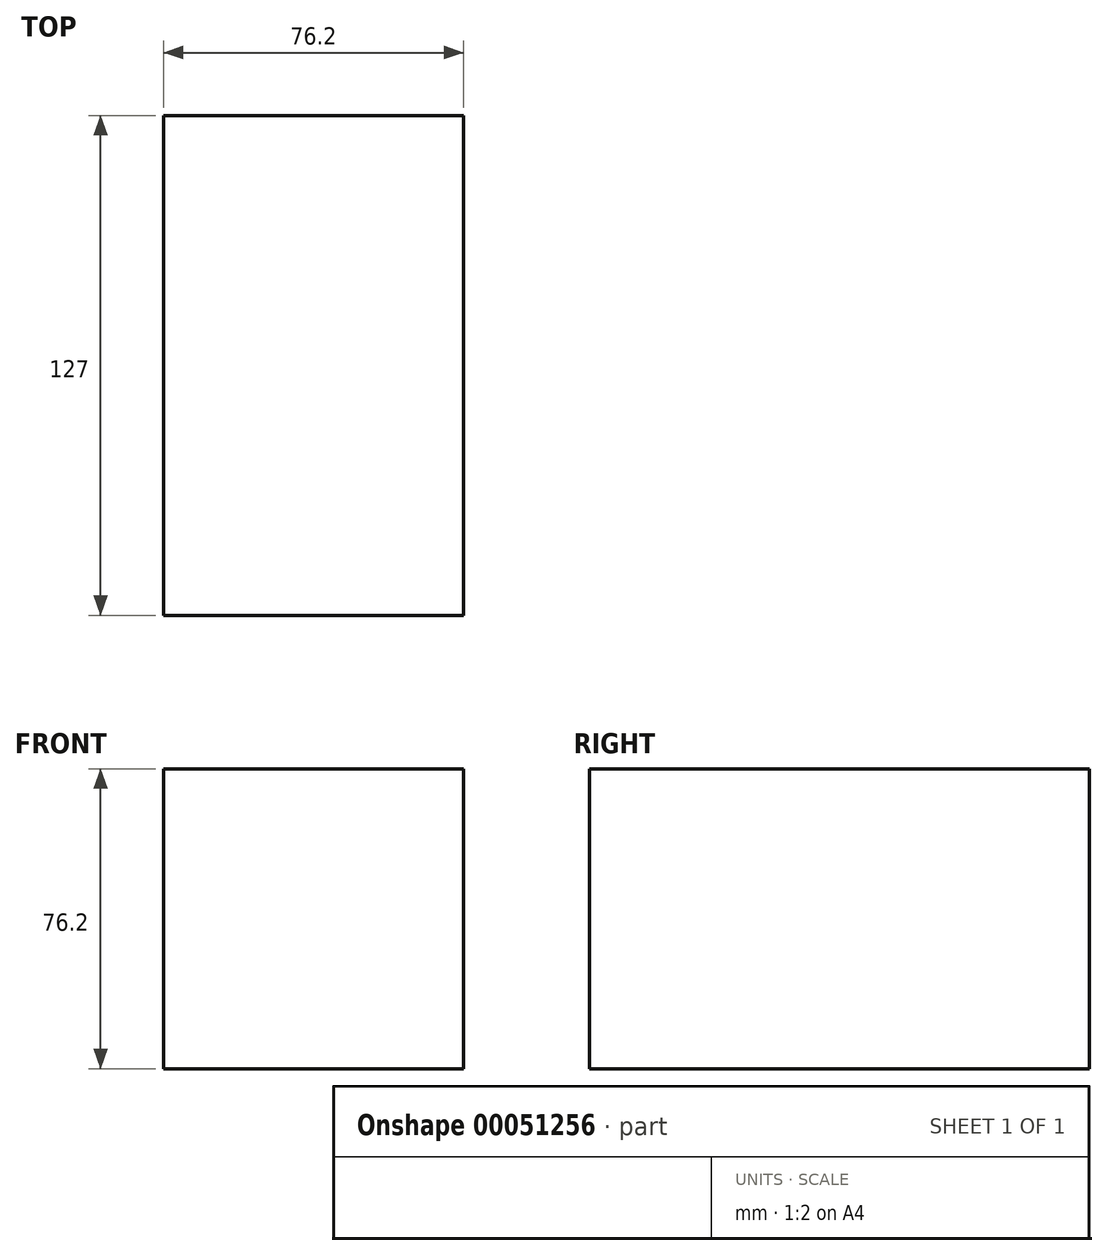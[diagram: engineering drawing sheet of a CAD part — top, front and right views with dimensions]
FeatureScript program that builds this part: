
annotation { "Feature Type Name" : "Feature", "Feature Type Description" : "" }
export const myFeature = defineFeature(function(context is Context, id is Id, definition is map)
    precondition{}
    {
        {
            var Q0;
            Q0=qCreatedBy(makeId("Top.planeOp"),FACE);
            var sketch = newSketch(context, id + "F0", { "sketchPlane" : qUnion([Q0])});
            skLineSegment(sketch, "E0.bottom", {"start": v(-65.07, 59.78) * mm, "end": v(11.13, 59.78) * mm});
            skLineSegment(sketch, "E0.top", {"start": v(-65.07, -67.22) * mm, "end": v(11.13, -67.22) * mm});
            skLineSegment(sketch, "E0.left", {"start": v(-65.07, 59.78) * mm, "end": v(-65.07, -67.22) * mm});
            skLineSegment(sketch, "E0.right", {"start": v(11.13, 59.78) * mm, "end": v(11.13, -67.22) * mm});
            skSolve(sketch);
        }
        {
            var Q0;
            Q0 = qSketchRegion(id + "F0", true);
            extrude(context, id + "F1", {"entities" : qUnion([Q0]), "depth" : 76.2 * mm});
        }
    });
